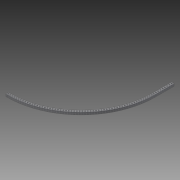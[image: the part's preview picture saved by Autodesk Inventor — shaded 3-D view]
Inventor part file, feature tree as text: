
AUTODESK INVENTOR PART (.ipt)
format: ipt  version: 2014 SP1 (Build 180222100, 222)  size: 248,832 bytes
history: native  units: in
note: dims shown in document units (in); Inventor stores cm internally (conversion verified against a paired STEP export)
features: extrude x3, sketch x3
ambient origin geometry x8: Origin, YZ Plane, XZ Plane, XY Plane, X Axis, Y Axis, Z Axis, Center Point
bodies: Solid1 (feature_tree)
feature tree (6):
  extrude  "Extrusion1"  Depth=28.0in
  extrude  "Extrusion5"  Depth=0.5in TaperAngle=0.0deg
  extrude  "Extrusion9"  Depth=0.3937in
  sketch  "Sketch1"  dims[d0=8.0in d2=28.0in]
  sketch  "Sketch5"  dims[d5=11.0in d7=0.5in d8=0.0in]
  sketch  "Sketch11"  dims[d46=0.925in d47=0.425in d67=4.5in d89=0.925in d93=0.5in d94=0.266in d95=0.25in d96=0.266in d97=0.266in d98=0.25in d99=0.25in d100=0.25in d101=0.25in d102=0.25in d103=4.0in d104=25.0in d105=4.0in d106=3.1496in d108=0.4688in d109=0.3937in d111=1.0in d113=3.937in d115=0.375in d116=0.3937in d118=1.0in d120=23.622in d122=90.0deg d124=2.5in d125=0.0in d142=3.75in d143=100.0in d144=0.0in]
